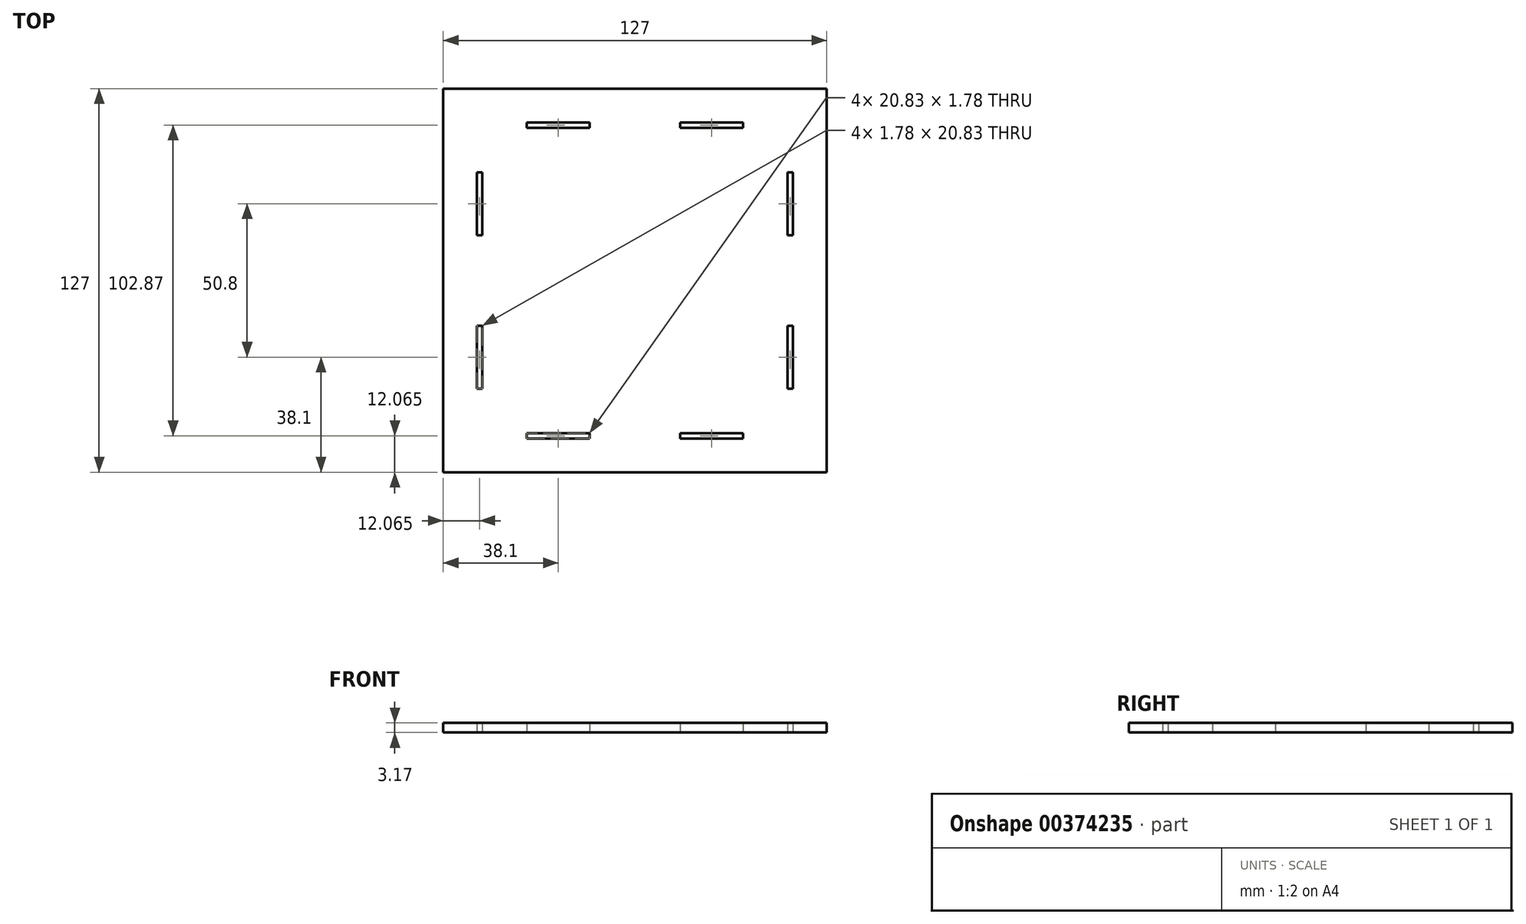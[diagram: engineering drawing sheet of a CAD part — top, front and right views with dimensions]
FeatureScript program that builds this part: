
annotation { "Feature Type Name" : "Feature", "Feature Type Description" : "" }
export const myFeature = defineFeature(function(context is Context, id is Id, definition is map)
    precondition{}
    {
        {
            var Q0;
            Q0=qCreatedBy(makeId("Top.planeOp"),FACE);
            var sketch = newSketch(context, id + "F0", { "sketchPlane" : qUnion([Q0])});
            skLineSegment(sketch, "E0", {"start": v(-63.5, -63.5) * mm, "end": v(63.5, -63.5) * mm});
            skLineSegment(sketch, "E1", {"start": v(63.5, -63.5) * mm, "end": v(63.5, 63.5) * mm});
            skLineSegment(sketch, "E2", {"start": v(63.5, 63.5) * mm, "end": v(-63.5, 63.5) * mm});
            skLineSegment(sketch, "E3", {"start": v(-63.5, 63.5) * mm, "end": v(-63.5, -63.5) * mm});
            skLineSegment(sketch, "E4", {"start": v(-35.81, 50.55) * mm, "end": v(-14.99, 50.55) * mm});
            skLineSegment(sketch, "E5", {"start": v(-14.99, 50.55) * mm, "end": v(-14.99, 52.32) * mm});
            skLineSegment(sketch, "E6", {"start": v(-14.99, 52.32) * mm, "end": v(-35.81, 52.32) * mm});
            skLineSegment(sketch, "E7", {"start": v(-35.81, 52.32) * mm, "end": v(-35.81, 50.55) * mm});
            skLineSegment(sketch, "E8", {"start": v(14.99, 50.55) * mm, "end": v(35.81, 50.55) * mm});
            skLineSegment(sketch, "E9", {"start": v(35.81, 50.55) * mm, "end": v(35.81, 52.32) * mm});
            skLineSegment(sketch, "E10", {"start": v(35.81, 52.32) * mm, "end": v(14.99, 52.32) * mm});
            skLineSegment(sketch, "E11", {"start": v(14.99, 52.32) * mm, "end": v(14.99, 50.55) * mm});
            skLineSegment(sketch, "E12", {"start": v(-35.81, -50.55) * mm, "end": v(-14.99, -50.55) * mm});
            skLineSegment(sketch, "E13", {"start": v(-14.99, -50.55) * mm, "end": v(-14.99, -52.32) * mm});
            skLineSegment(sketch, "E14", {"start": v(-14.99, -52.32) * mm, "end": v(-35.81, -52.32) * mm});
            skLineSegment(sketch, "E15", {"start": v(-35.81, -52.32) * mm, "end": v(-35.81, -50.55) * mm});
            skLineSegment(sketch, "E16", {"start": v(14.99, -50.55) * mm, "end": v(35.81, -50.55) * mm});
            skLineSegment(sketch, "E17", {"start": v(35.81, -50.55) * mm, "end": v(35.81, -52.32) * mm});
            skLineSegment(sketch, "E18", {"start": v(35.81, -52.32) * mm, "end": v(14.99, -52.32) * mm});
            skLineSegment(sketch, "E19", {"start": v(14.99, -52.32) * mm, "end": v(14.99, -50.55) * mm});
            skLineSegment(sketch, "E20", {"start": v(-52.32, -35.81) * mm, "end": v(-50.55, -35.81) * mm});
            skLineSegment(sketch, "E21", {"start": v(-50.55, -35.81) * mm, "end": v(-50.55, -14.99) * mm});
            skLineSegment(sketch, "E22", {"start": v(-50.55, -14.99) * mm, "end": v(-52.32, -14.99) * mm});
            skLineSegment(sketch, "E23", {"start": v(-52.32, -14.99) * mm, "end": v(-52.32, -35.81) * mm});
            skLineSegment(sketch, "E24", {"start": v(-52.32, 35.81) * mm, "end": v(-50.55, 35.81) * mm});
            skLineSegment(sketch, "E25", {"start": v(-50.55, 35.81) * mm, "end": v(-50.55, 14.99) * mm});
            skLineSegment(sketch, "E26", {"start": v(-50.55, 14.99) * mm, "end": v(-52.32, 14.99) * mm});
            skLineSegment(sketch, "E27", {"start": v(-52.32, 14.99) * mm, "end": v(-52.32, 35.81) * mm});
            skLineSegment(sketch, "E28", {"start": v(52.32, -35.81) * mm, "end": v(50.55, -35.81) * mm});
            skLineSegment(sketch, "E29", {"start": v(50.55, -35.81) * mm, "end": v(50.55, -14.99) * mm});
            skLineSegment(sketch, "E30", {"start": v(50.55, -14.99) * mm, "end": v(52.32, -14.99) * mm});
            skLineSegment(sketch, "E31", {"start": v(52.32, -14.99) * mm, "end": v(52.32, -35.81) * mm});
            skLineSegment(sketch, "E32", {"start": v(52.32, 35.81) * mm, "end": v(50.55, 35.81) * mm});
            skLineSegment(sketch, "E33", {"start": v(50.55, 35.81) * mm, "end": v(50.55, 14.99) * mm});
            skLineSegment(sketch, "E34", {"start": v(50.55, 14.99) * mm, "end": v(52.32, 14.99) * mm});
            skLineSegment(sketch, "E35", {"start": v(52.32, 14.99) * mm, "end": v(52.32, 35.81) * mm});
            skSolve(sketch);
        }
        {
            var Q0;
            Q0=makeQuery(id+"F0.imprint","IMPRINT",FACE,{"disambiguationData":[TD([[makeQuery(id+"F0.imprint","IMPRINT",EDGE,{"derivedFrom":sQuery(id+"F0.wireOp",EDGE,"E0")}),1.0]])]});
            extrude(context, id + "F1", {"entities" : qUnion([Q0]), "depth" : 3.17 * mm});
        }
    });
